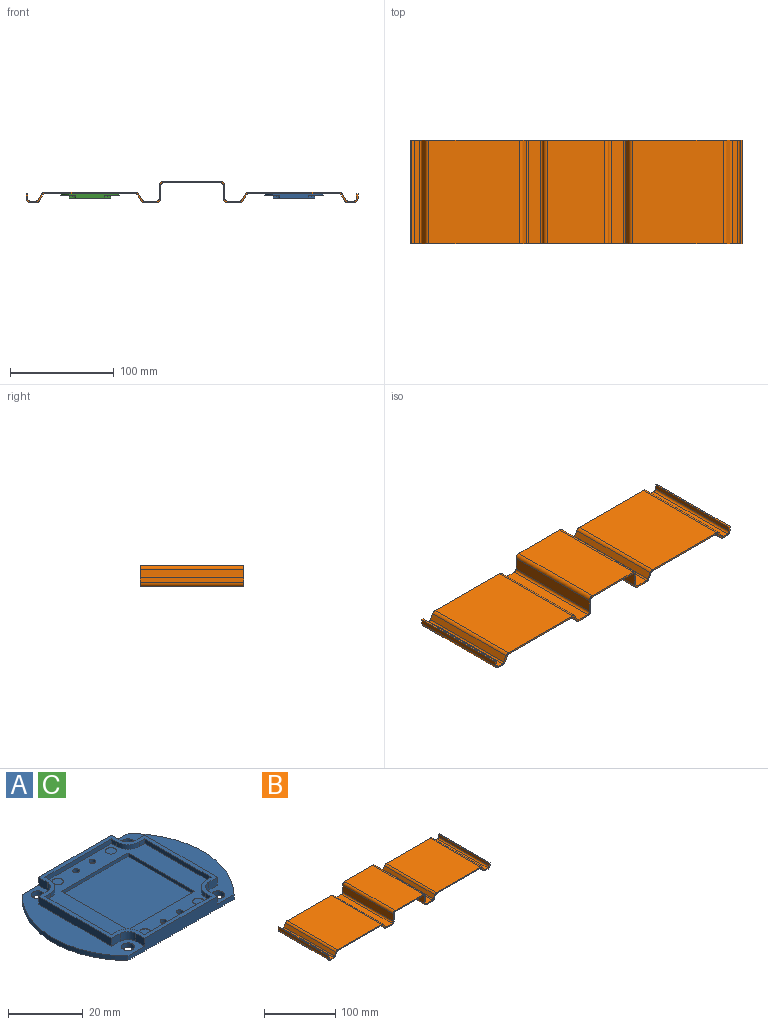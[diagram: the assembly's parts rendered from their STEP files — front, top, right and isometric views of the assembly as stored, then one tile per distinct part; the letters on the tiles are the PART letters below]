
ASSEMBLY  parts=3 mates=2
PART A: 64 faces, bbox 56.6x40x4.1 mm
  f0: plane 37.6x37.6mm, normal (0,0,1), area 608.6mm2, adj f25,f26,f27,f28,f29,f30,f31,f32
  f1: plane 40x14.53mm, normal (0,0,1), area 283.3mm2, adj f3,f5,f7,f8,f9,f17,f18,f19
  f2: plane 40x14.53mm, normal (0,0,1), area 283.3mm2, adj f3,f4,f5,f6,f10,f12,f13,f14
  f3: plane 40x4.1mm, normal (0,-1,0), area 131.5mm2, adj f1,f2,f4,f9,f11,f23,f24,f42
  f4: cylinder r=28.28mm len=40mm, axis (0,0,1), area 66.6mm2, adj f2,f3,f5,f11
  f5: plane 40x4.1mm, normal (0,1,0), area 131.5mm2, adj f1,f2,f4,f9,f11,f16,f17,f42
  f6: cylinder r=1.75mm len=3.5mm, axis (0,0,1), area 16.5mm2, adj f2,f11
  f7: cylinder r=1.75mm len=3.5mm, axis (0,0,1), area 16.5mm2, adj f1,f11
  f8: cylinder r=1.75mm len=3.5mm, axis (0,0,1), area 16.5mm2, adj f1,f11
  f9: cylinder r=28.28mm len=40mm, axis (0,0,1), area 66.6mm2, adj f1,f3,f5,f11
  f10: cylinder r=1.75mm len=3.5mm, axis (0,0,1), area 16.5mm2, adj f2,f11
  f11: plane 56.57x40mm, normal (0,0,-1), area 2018.2mm2, adj f3,f4,f5,f6,f7,f8,f9,f10
  f12: plane 3.25x2.6mm, normal (0,-1,0), area 8.4mm2, adj f2,f13,f41,f42
  f13: plane 27.5x2.6mm, normal (1,0,0), area 71.5mm2, adj f2,f12,f14,f42
  f14: plane 3.25x2.6mm, normal (0,1,0), area 8.4mm2, adj f2,f13,f15,f42
  f15: cylinder r=3mm len=3mm, axis (0,0,-1), area 12.3mm2, adj f2,f14,f16,f42
  f16: plane 3.25x2.6mm, normal (1,0,0), area 8.4mm2, adj f2,f5,f15,f42
  f17: plane 3.25x2.6mm, normal (-1,0,0), area 8.4mm2, adj f1,f5,f18,f42
  f18: cylinder r=3mm len=3mm, axis (0,0,-1), area 12.3mm2, adj f1,f17,f19,f42
  f19: plane 3.25x2.6mm, normal (0,1,0), area 8.4mm2, adj f1,f18,f20,f42
  f20: plane 27.5x2.6mm, normal (-1,0,0), area 71.5mm2, adj f1,f19,f21,f42
  f21: plane 3.25x2.6mm, normal (0,-1,0), area 8.4mm2, adj f1,f20,f22,f42
  f22: cylinder r=3mm len=3mm, axis (0,0,-1), area 12.3mm2, adj f1,f21,f23,f42
  f23: plane 3.25x2.6mm, normal (-1,0,0), area 8.4mm2, adj f1,f3,f22,f42
  f24: plane 3.25x2.6mm, normal (1,0,0), area 8.4mm2, adj f2,f3,f41,f42
  f25: plane 2.05x1.5mm, normal (0,1,0), area 3.1mm2, adj f0,f26,f40,f42
  f26: cylinder r=4.2mm len=4.2mm, axis (0,0,-1), area 9.9mm2, adj f0,f25,f27,f42
  f27: plane 2.05x1.5mm, normal (-1,0,0), area 3.1mm2, adj f0,f26,f28,f42
  f28: plane 25.1x1.5mm, normal (0,1,0), area 37.6mm2, adj f0,f27,f29,f42
  f29: plane 2.05x1.5mm, normal (1,0,0), area 3.1mm2, adj f0,f28,f30,f42
  f30: cylinder r=4.2mm len=4.2mm, axis (0,0,-1), area 9.9mm2, adj f0,f29,f31,f42
  f31: plane 2.05x1.5mm, normal (0,1,0), area 3.1mm2, adj f0,f30,f32,f42
  f32: plane 25.1x1.5mm, normal (1,0,0), area 37.6mm2, adj f0,f31,f33,f42
  f33: plane 2.05x1.5mm, normal (0,-1,0), area 3.1mm2, adj f0,f32,f34,f42
  f34: cylinder r=4.2mm len=4.2mm, axis (0,0,-1), area 9.9mm2, adj f0,f33,f35,f42
  f35: plane 2.05x1.5mm, normal (1,0,0), area 3.1mm2, adj f0,f34,f36,f42
  f36: plane 25.1x1.5mm, normal (0,-1,0), area 37.6mm2, adj f0,f35,f37,f42
  f37: plane 2.05x1.5mm, normal (-1,0,0), area 3.1mm2, adj f0,f36,f38,f42
  f38: cylinder r=4.2mm len=4.2mm, axis (0,0,-1), area 9.9mm2, adj f0,f37,f39,f42
  f39: plane 2.05x1.5mm, normal (0,-1,0), area 3.1mm2, adj f0,f38,f40,f42
  f40: plane 25.1x1.5mm, normal (-1,0,0), area 37.6mm2, adj f0,f25,f39,f42
  f41: cylinder r=3mm len=3mm, axis (0,0,-1), area 12.3mm2, adj f2,f12,f24,f42
  f42: plane 40x40mm, normal (0,0,1), area 178.8mm2, adj f3,f5,f12,f13,f14,f15,f16,f17
  f43: plane 25x1.1mm, normal (0,-1,0), area 27.5mm2, adj f0,f44,f50,f51
  f44: plane 25x1.1mm, normal (-1,0,0), area 27.5mm2, adj f0,f43,f45,f51
  f45: plane 25x1.1mm, normal (0,1,0), area 27.5mm2, adj f0,f44,f50,f51
  f46: cylinder r=0.93mm len=1.85mm, axis (0,0,-1), area 6.4mm2, adj f0,f55
  f47: cylinder r=0.93mm len=1.85mm, axis (0,0,-1), area 6.4mm2, adj f0,f54
  f48: cylinder r=0.93mm len=1.85mm, axis (0,0,-1), area 6.4mm2, adj f0,f53
  f49: cylinder r=0.93mm len=1.85mm, axis (0,0,-1), area 6.4mm2, adj f0,f52
  f50: plane 25x1.1mm, normal (1,0,0), area 27.5mm2, adj f0,f43,f45,f51
  f51: plane 25x25mm, normal (0,0,1), area 625mm2, adj f43,f44,f45,f50
  f52: plane 1.85x1.85mm, normal (0,0,1), area 2.7mm2, adj f49
  f53: plane 1.85x1.85mm, normal (0,0,1), area 2.7mm2, adj f48
  f54: plane 1.85x1.85mm, normal (0,0,1), area 2.7mm2, adj f47
  f55: plane 1.85x1.85mm, normal (0,0,1), area 2.7mm2, adj f46
  f56: cylinder r=1.5mm len=3mm, axis (0,0,1), area 0.9mm2, adj f0,f57
  f57: plane 3x3mm, normal (0,0,1), area 7.1mm2, adj f56
  f58: cylinder r=1.5mm len=3mm, axis (0,0,1), area 0.9mm2, adj f0,f59
  f59: plane 3x3mm, normal (0,0,1), area 7.1mm2, adj f58
  f60: cylinder r=1.5mm len=3mm, axis (0,0,1), area 0.9mm2, adj f0,f61
  f61: plane 3x3mm, normal (0,0,1), area 7.1mm2, adj f60
  f62: cylinder r=1.5mm len=3mm, axis (0,0,1), area 0.9mm2, adj f0,f63
  f63: plane 3x3mm, normal (0,0,1), area 7.1mm2, adj f62
PART B: 118 faces, bbox 319.8x100x20.6 mm
  f0: plane 55.6x1.6mm, normal (0,1,0), area 89mm2, adj f2,f3,f5,f9
  f1: plane 55.6x1.6mm, normal (0,-1,0), area 89mm2, adj f2,f3,f4,f8
  f2: plane 100x55.6mm, normal (0,0,1), area 5559.9mm2, adj f0,f1,f6,f10
  f3: plane 100x55.6mm, normal (0,0,-1), area 5559.9mm2, adj f0,f1,f7,f11
  f4: plane 3.9x3.9mm, normal (0,-1,0), area 7.8mm2, adj f1,f6,f7,f13
  f5: plane 3.9x3.9mm, normal (0,1,0), area 7.8mm2, adj f0,f6,f7,f12
  f6: cylinder r=3.9mm len=100mm, axis (0,-1,0), area 612.6mm2, adj f2,f4,f5,f14
  f7: cylinder r=2.3mm len=100mm, axis (0,-1,0), area 361.3mm2, adj f3,f4,f5,f15
  f8: plane 3.9x3.9mm, normal (0,-1,0), area 7.8mm2, adj f1,f10,f11,f21
  f9: plane 3.9x3.9mm, normal (0,1,0), area 7.8mm2, adj f0,f10,f11,f20
  f10: cylinder r=3.9mm len=100mm, axis (0,-1,0), area 612.6mm2, adj f2,f8,f9,f22
  f11: cylinder r=2.3mm len=100mm, axis (0,-1,0), area 361.3mm2, adj f3,f8,f9,f23
  f12: plane 12.8x1.6mm, normal (0,1,0), area 20.5mm2, adj f5,f14,f15,f17
  f13: plane 12.8x1.6mm, normal (0,-1,0), area 20.5mm2, adj f4,f14,f15,f16
  f14: plane 100x12.8mm, normal (-1,0,0), area 1280mm2, adj f6,f12,f13,f19
  f15: plane 100x12.8mm, normal (1,0,0), area 1280mm2, adj f7,f12,f13,f18
  f16: plane 3.9x3.9mm, normal (0,-1,0), area 7.8mm2, adj f13,f18,f19,f25
  f17: plane 3.9x3.9mm, normal (0,1,0), area 7.8mm2, adj f12,f18,f19,f24
  f18: cylinder r=3.9mm len=100mm, axis (0,-1,0), area 612.6mm2, adj f15,f16,f17,f27
  f19: cylinder r=2.3mm len=100mm, axis (0,-1,0), area 361.3mm2, adj f14,f16,f17,f26
  f20: plane 12.8x1.6mm, normal (0,1,0), area 20.5mm2, adj f9,f22,f23,f29
  f21: plane 12.8x1.6mm, normal (0,-1,0), area 20.5mm2, adj f8,f22,f23,f28
  f22: plane 100x12.8mm, normal (1,0,0), area 1280mm2, adj f10,f20,f21,f31
  f23: plane 100x12.8mm, normal (-1,0,0), area 1280mm2, adj f11,f20,f21,f30
  f24: plane 11.97x1.6mm, normal (0,1,0), area 19.2mm2, adj f17,f26,f27,f33
  f25: plane 11.97x1.6mm, normal (0,-1,0), area 19.2mm2, adj f16,f26,f27,f32
  f26: plane 100x11.97mm, normal (0,0,1), area 1197.4mm2, adj f19,f24,f25,f35
  f27: plane 100x11.97mm, normal (0,0,-1), area 1197.4mm2, adj f18,f24,f25,f34
  f28: plane 3.9x3.9mm, normal (0,-1,0), area 7.8mm2, adj f21,f30,f31,f45
  f29: plane 3.9x3.9mm, normal (0,1,0), area 7.8mm2, adj f20,f30,f31,f44
  f30: cylinder r=3.9mm len=100mm, axis (0,-1,0), area 612.6mm2, adj f23,f28,f29,f47
  f31: cylinder r=2.3mm len=100mm, axis (0,-1,0), area 361.3mm2, adj f22,f28,f29,f46
  f32: plane 3.38x2.75mm, normal (0,-1,0), area 5.2mm2, adj f25,f34,f35,f37
  f33: plane 3.38x2.75mm, normal (0,1,0), area 5.2mm2, adj f24,f34,f35,f36
  f34: cylinder r=3.9mm len=100mm, axis (0,-1,0), area 408.4mm2, adj f27,f32,f33,f39
  f35: cylinder r=2.3mm len=100mm, axis (0,-1,0), area 240.9mm2, adj f26,f32,f33,f38
  f36: plane 6.3x4.56mm, normal (0,1,0), area 10.2mm2, adj f33,f38,f39,f41
  f37: plane 6.3x4.56mm, normal (0,-1,0), area 10.2mm2, adj f32,f38,f39,f40
  f38: plane 100x5.5mm, normal (0.87,0,0.5), area 635.1mm2, adj f35,f36,f37,f42
  f39: plane 100x5.5mm, normal (-0.87,0,-0.5), area 635.1mm2, adj f34,f36,f37,f43
  f40: plane 3.38x2.75mm, normal (0,-1,0), area 5.2mm2, adj f37,f42,f43,f49
  f41: plane 3.38x2.75mm, normal (0,1,0), area 5.2mm2, adj f36,f42,f43,f48
  f42: cylinder r=3.9mm len=100mm, axis (0,-1,0), area 408.4mm2, adj f38,f40,f41,f50
  f43: cylinder r=2.3mm len=100mm, axis (0,-1,0), area 240.9mm2, adj f39,f40,f41,f51
  f44: plane 11.97x1.6mm, normal (0,1,0), area 19.2mm2, adj f29,f46,f47,f86
  f45: plane 11.97x1.6mm, normal (0,-1,0), area 19.2mm2, adj f28,f46,f47,f85
  f46: plane 100x11.97mm, normal (0,0,1), area 1197.4mm2, adj f31,f44,f45,f88
  f47: plane 100x11.97mm, normal (0,0,-1), area 1197.4mm2, adj f30,f44,f45,f87
  f48: plane 87.24x1.6mm, normal (0,1,0), area 139.6mm2, adj f41,f50,f51,f74
  f49: plane 87.24x1.6mm, normal (0,-1,0), area 139.6mm2, adj f40,f50,f51,f73
  f50: plane 100x87.24mm, normal (0,0,1), area 8724.4mm2, adj f42,f48,f49,f75
  f51: plane 100x87.24mm, normal (0,0,-1), area 8724.4mm2, adj f43,f48,f49,f76
  f52: plane 4.7x1.6mm, normal (0,1,0), area 7.5mm2, adj f53,f55,f56,f58
  f53: plane 100x1.6mm, normal (0,0,1), area 160mm2, adj f52,f54,f55,f56
  f54: plane 4.7x1.6mm, normal (0,-1,0), area 7.5mm2, adj f53,f55,f56,f57
  f55: plane 100x4.7mm, normal (1,0,0), area 470mm2, adj f52,f53,f54,f60
  f56: plane 100x4.7mm, normal (-1,0,0), area 470mm2, adj f52,f53,f54,f59
  f57: plane 3.9x3.9mm, normal (0,-1,0), area 7.8mm2, adj f54,f59,f60,f62
  f58: plane 3.9x3.9mm, normal (0,1,0), area 7.8mm2, adj f52,f59,f60,f61
  f59: cylinder r=3.9mm len=100mm, axis (0,-1,0), area 612.6mm2, adj f56,f57,f58,f64
  f60: cylinder r=2.3mm len=100mm, axis (0,-1,0), area 361.3mm2, adj f55,f57,f58,f63
  f61: plane 5.7x1.6mm, normal (0,1,0), area 9.1mm2, adj f58,f63,f64,f66
  f62: plane 5.7x1.6mm, normal (0,-1,0), area 9.1mm2, adj f57,f63,f64,f65
  f63: plane 100x5.7mm, normal (0,0,1), area 569.9mm2, adj f60,f61,f62,f68
  f64: plane 100x5.7mm, normal (0,0,-1), area 569.9mm2, adj f59,f61,f62,f67
  f65: plane 3.38x2.75mm, normal (0,-1,0), area 5.2mm2, adj f62,f67,f68,f70
  f66: plane 3.38x2.75mm, normal (0,1,0), area 5.2mm2, adj f61,f67,f68,f69
  f67: cylinder r=3.9mm len=100mm, axis (0,-1,0), area 408.4mm2, adj f64,f65,f66,f72
  f68: cylinder r=2.3mm len=100mm, axis (0,-1,0), area 240.9mm2, adj f63,f65,f66,f71
  f69: plane 6.3x4.56mm, normal (0,1,0), area 10.2mm2, adj f66,f71,f72,f74
  f70: plane 6.3x4.56mm, normal (0,-1,0), area 10.2mm2, adj f65,f71,f72,f73
  f71: plane 100x5.5mm, normal (-0.87,0,0.5), area 635.1mm2, adj f68,f69,f70,f75
  f72: plane 100x5.5mm, normal (0.87,0,-0.5), area 635.1mm2, adj f67,f69,f70,f76
  f73: plane 3.38x2.75mm, normal (0,-1,0), area 5.2mm2, adj f49,f70,f75,f76
  f74: plane 3.38x2.75mm, normal (0,1,0), area 5.2mm2, adj f48,f69,f75,f76
  f75: cylinder r=3.9mm len=100mm, axis (0,-1,0), area 408.4mm2, adj f50,f71,f73,f74
  f76: cylinder r=2.3mm len=100mm, axis (0,-1,0), area 240.9mm2, adj f51,f72,f73,f74
  f77: plane 3.38x2.75mm, normal (0,-1,0), area 5.2mm2, adj f79,f80,f82,f90
  f78: plane 3.38x2.75mm, normal (0,1,0), area 5.2mm2, adj f79,f80,f81,f89
  f79: cylinder r=3.9mm len=100mm, axis (0,-1,0), area 408.4mm2, adj f77,f78,f83,f91
  f80: cylinder r=2.3mm len=100mm, axis (0,-1,0), area 240.9mm2, adj f77,f78,f84,f92
  f81: plane 6.3x4.56mm, normal (0,1,0), area 10.2mm2, adj f78,f83,f84,f86
  f82: plane 6.3x4.56mm, normal (0,-1,0), area 10.2mm2, adj f77,f83,f84,f85
  f83: plane 100x5.5mm, normal (-0.87,0,0.5), area 635.1mm2, adj f79,f81,f82,f88
  f84: plane 100x5.5mm, normal (0.87,0,-0.5), area 635.1mm2, adj f80,f81,f82,f87
  f85: plane 3.38x2.75mm, normal (0,-1,0), area 5.2mm2, adj f45,f82,f87,f88
  f86: plane 3.38x2.75mm, normal (0,1,0), area 5.2mm2, adj f44,f81,f87,f88
  f87: cylinder r=3.9mm len=100mm, axis (0,-1,0), area 408.4mm2, adj f47,f84,f85,f86
  f88: cylinder r=2.3mm len=100mm, axis (0,-1,0), area 240.9mm2, adj f46,f83,f85,f86
  f89: plane 87.24x1.6mm, normal (0,1,0), area 139.6mm2, adj f78,f91,f92,f115
  f90: plane 87.24x1.6mm, normal (0,-1,0), area 139.6mm2, adj f77,f91,f92,f114
  f91: plane 100x87.24mm, normal (0,0,1), area 8724.4mm2, adj f79,f89,f90,f116
  f92: plane 100x87.24mm, normal (0,0,-1), area 8724.4mm2, adj f80,f89,f90,f117
  f93: plane 4.7x1.6mm, normal (0,1,0), area 7.5mm2, adj f95,f96,f97,f99
  f94: plane 4.7x1.6mm, normal (0,-1,0), area 7.5mm2, adj f95,f96,f97,f98
  f95: plane 100x1.6mm, normal (0,0,1), area 160mm2, adj f93,f94,f96,f97
  f96: plane 100x4.7mm, normal (-1,0,0), area 470mm2, adj f93,f94,f95,f101
  f97: plane 100x4.7mm, normal (1,0,0), area 470mm2, adj f93,f94,f95,f100
  f98: plane 3.9x3.9mm, normal (0,-1,0), area 7.8mm2, adj f94,f100,f101,f103
  f99: plane 3.9x3.9mm, normal (0,1,0), area 7.8mm2, adj f93,f100,f101,f102
  f100: cylinder r=3.9mm len=100mm, axis (0,-1,0), area 612.6mm2, adj f97,f98,f99,f105
  f101: cylinder r=2.3mm len=100mm, axis (0,-1,0), area 361.3mm2, adj f96,f98,f99,f104
  f102: plane 5.7x1.6mm, normal (0,1,0), area 9.1mm2, adj f99,f104,f105,f107
  f103: plane 5.7x1.6mm, normal (0,-1,0), area 9.1mm2, adj f98,f104,f105,f106
  f104: plane 100x5.7mm, normal (0,0,1), area 569.9mm2, adj f101,f102,f103,f109
  f105: plane 100x5.7mm, normal (0,0,-1), area 569.9mm2, adj f100,f102,f103,f108
  f106: plane 3.38x2.75mm, normal (0,-1,0), area 5.2mm2, adj f103,f108,f109,f111
  f107: plane 3.38x2.75mm, normal (0,1,0), area 5.2mm2, adj f102,f108,f109,f110
  f108: cylinder r=3.9mm len=100mm, axis (0,-1,0), area 408.4mm2, adj f105,f106,f107,f113
  f109: cylinder r=2.3mm len=100mm, axis (0,-1,0), area 240.9mm2, adj f104,f106,f107,f112
  f110: plane 6.3x4.56mm, normal (0,1,0), area 10.2mm2, adj f107,f112,f113,f115
  f111: plane 6.3x4.56mm, normal (0,-1,0), area 10.2mm2, adj f106,f112,f113,f114
  f112: plane 100x5.5mm, normal (0.87,0,0.5), area 635.1mm2, adj f109,f110,f111,f116
  f113: plane 100x5.5mm, normal (-0.87,0,-0.5), area 635.1mm2, adj f108,f110,f111,f117
  f114: plane 3.38x2.75mm, normal (0,-1,0), area 5.2mm2, adj f90,f111,f116,f117
  f115: plane 3.38x2.75mm, normal (0,1,0), area 5.2mm2, adj f89,f110,f116,f117
  f116: cylinder r=3.9mm len=100mm, axis (0,-1,0), area 408.4mm2, adj f91,f112,f114,f115
  f117: cylinder r=2.3mm len=100mm, axis (0,-1,0), area 240.9mm2, adj f92,f113,f114,f115
PART C: same geometry as A
PLACE A rot(axis=(1,0,0),180deg) t=(103.46,0,0.61)mm
PLACE B at identity fixed
PLACE C rot(axis=(1,0,0),180deg) t=(-92.82,0,0.61)mm
MATE fastened A.f4 <-> B.f92  axis (0,0,1) through (103.46,0,2.11)mm
MATE fastened C.f4 <-> B.f51  axis (0,0,1) through (-92.82,0,2.11)mm
